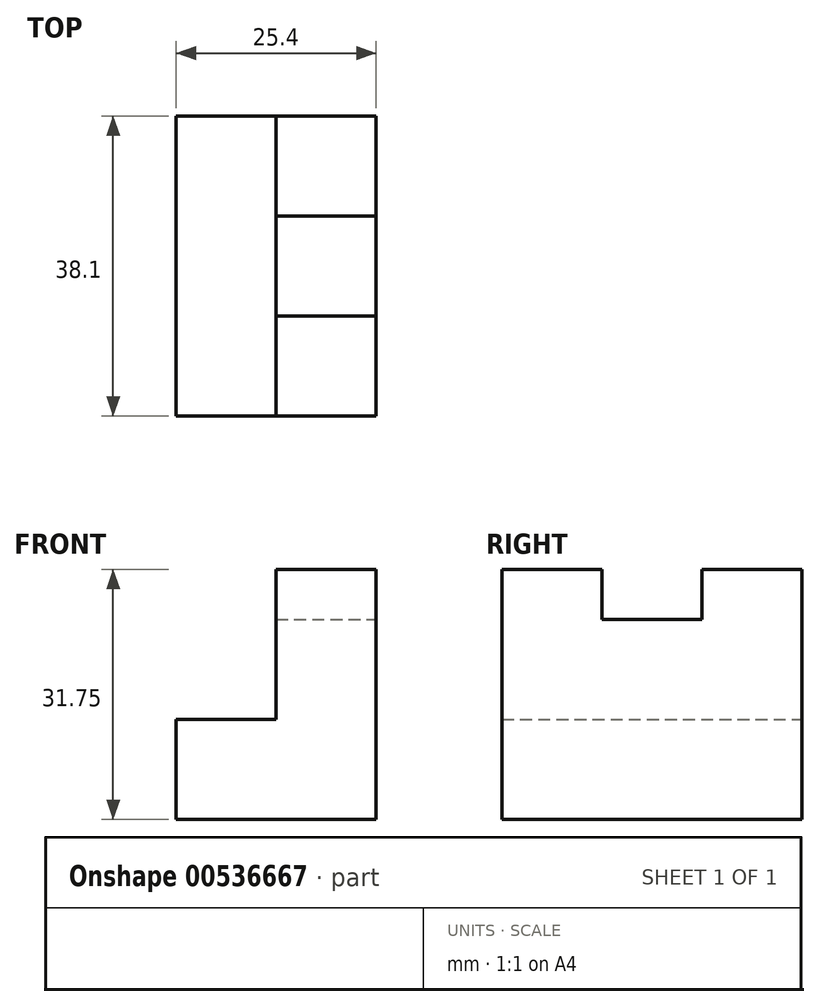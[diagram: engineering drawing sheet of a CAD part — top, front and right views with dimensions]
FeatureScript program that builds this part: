
annotation { "Feature Type Name" : "Feature", "Feature Type Description" : "" }
export const myFeature = defineFeature(function(context is Context, id is Id, definition is map)
    precondition{}
    {
        {
            var Q0;
            Q0=qCreatedBy(makeId("Front.planeOp"),FACE);
            var sketch = newSketch(context, id + "F0", { "sketchPlane" : qUnion([Q0])});
            skLineSegment(sketch, "E0", {"start": v(-43.86, 57.1) * mm, "end": v(-43.86, 38.05) * mm});
            skLineSegment(sketch, "E1", {"start": v(-43.86, 38.05) * mm, "end": v(-56.56, 38.05) * mm});
            skLineSegment(sketch, "E2", {"start": v(-56.56, 38.05) * mm, "end": v(-56.56, 25.35) * mm});
            skLineSegment(sketch, "E3", {"start": v(-56.56, 25.35) * mm, "end": v(-31.16, 25.35) * mm});
            skLineSegment(sketch, "E4", {"start": v(-31.16, 25.35) * mm, "end": v(-31.16, 57.1) * mm});
            skLineSegment(sketch, "E5", {"start": v(-31.16, 57.1) * mm, "end": v(-43.86, 57.1) * mm});
            skSolve(sketch);
        }
        {
            var Q0;
            Q0=makeQuery(id+"F0.imprint","IMPRINT",FACE,{"disambiguationData":[TD([[makeQuery(id+"F0.imprint","IMPRINT",EDGE,{"derivedFrom":sQuery(id+"F0.wireOp",EDGE,"E0")}),1.0]])]});
            extrude(context, id + "F1", {"entities" : qUnion([Q0]), "depth" : 38.1 * mm, "offsetDistance" : 25.4 * mm});
        }
        {
            var Q0;
            Q0=makeQuery(id+"F1.opExtrude","SWEPT_FACE",FACE,{"disambiguationData":[OSD([sQuery(id+"F0.wireOp",EDGE,"E4")])]});
            var sketch = newSketch(context, id + "F2", { "sketchPlane" : qUnion([Q0])});
            skLineSegment(sketch, "E6", {"start": v(-25.4, 57.1) * mm, "end": v(-25.4, 50.75) * mm});
            skLineSegment(sketch, "E7", {"start": v(-25.4, 50.75) * mm, "end": v(-12.7, 50.75) * mm});
            skLineSegment(sketch, "E8", {"start": v(-12.7, 50.75) * mm, "end": v(-12.7, 57.1) * mm});
            skSolve(sketch);
        }
        {
            var Q0;
            Q0 = qSketchRegion(id + "F2", true);
            var Q1;
            {var subQ0=sQuery(id+"F2.wireOp",EDGE,"E6");Q1=makeQuery(id+"F2.imprint","IMPRINT",FACE,{"disambiguationData":[TD([[makeQuery(id+"F2.imprint","IMPRINT",EDGE,{"derivedFrom":subQ0}),1.0]])]});}
            extrude(context, id + "F3", {"entities" : qUnion([Q0, Q1]), "operationType" : NewBodyOperationType.REMOVE, "oppositeDirection" : true, "depth" : 25.4 * mm, "offsetDistance" : 25.4 * mm});
        }
    });
